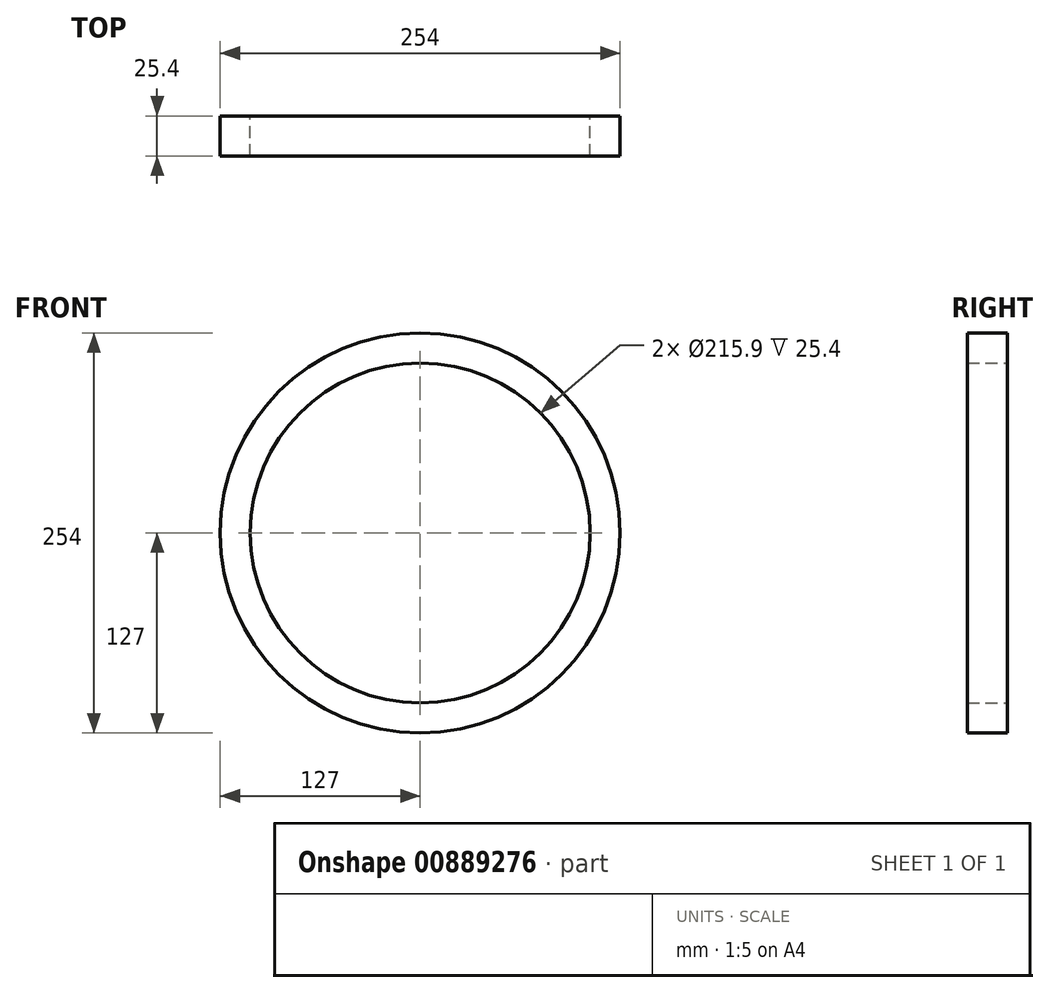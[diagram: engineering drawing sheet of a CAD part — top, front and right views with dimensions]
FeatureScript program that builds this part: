
annotation { "Feature Type Name" : "Feature", "Feature Type Description" : "" }
export const myFeature = defineFeature(function(context is Context, id is Id, definition is map)
    precondition{}
    {
        {
            var Q0;
            Q0=qCreatedBy(makeId("Front.planeOp"),FACE);
            var sketch = newSketch(context, id + "F0", { "sketchPlane" : qUnion([Q0])});
            skCircle(sketch, "E0", {"center": v(0, 0) * mm, "radius": 127 * mm});
            skCircle(sketch, "E1", {"center": v(0, 0) * mm, "radius": 107.95 * mm});
            skSolve(sketch);
        }
        {
            var Q0;
            Q0=makeQuery(id+"F0.imprint","IMPRINT",FACE,{"disambiguationData":[TD([[makeQuery(id+"F0.imprint","IMPRINT",EDGE,{"derivedFrom":sQuery(id+"F0.wireOp",EDGE,"E0")}),1.0]])]});
            var sketch = newSketch(context, id + "F1", { "sketchPlane" : qUnion([Q0])});
            skSolve(sketch);
        }
        {
            var Q0;
            Q0=makeQuery(id+"F1.imprint","IMPRINT",FACE,{"disambiguationData":[TD([[makeQuery(id+"F1.imprint","IMPRINT",EDGE,{"derivedFrom":makeQuery(id+"F0.imprint","IMPRINT",EDGE,{"derivedFrom":sQuery(id+"F0.wireOp",EDGE,"E0")})}),1.0]])]});
            extrude(context, id + "F2", {"entities" : qUnion([Q0]), "depth" : 25.4 * mm, "offsetDistance" : 25.4 * mm});
        }
    });
